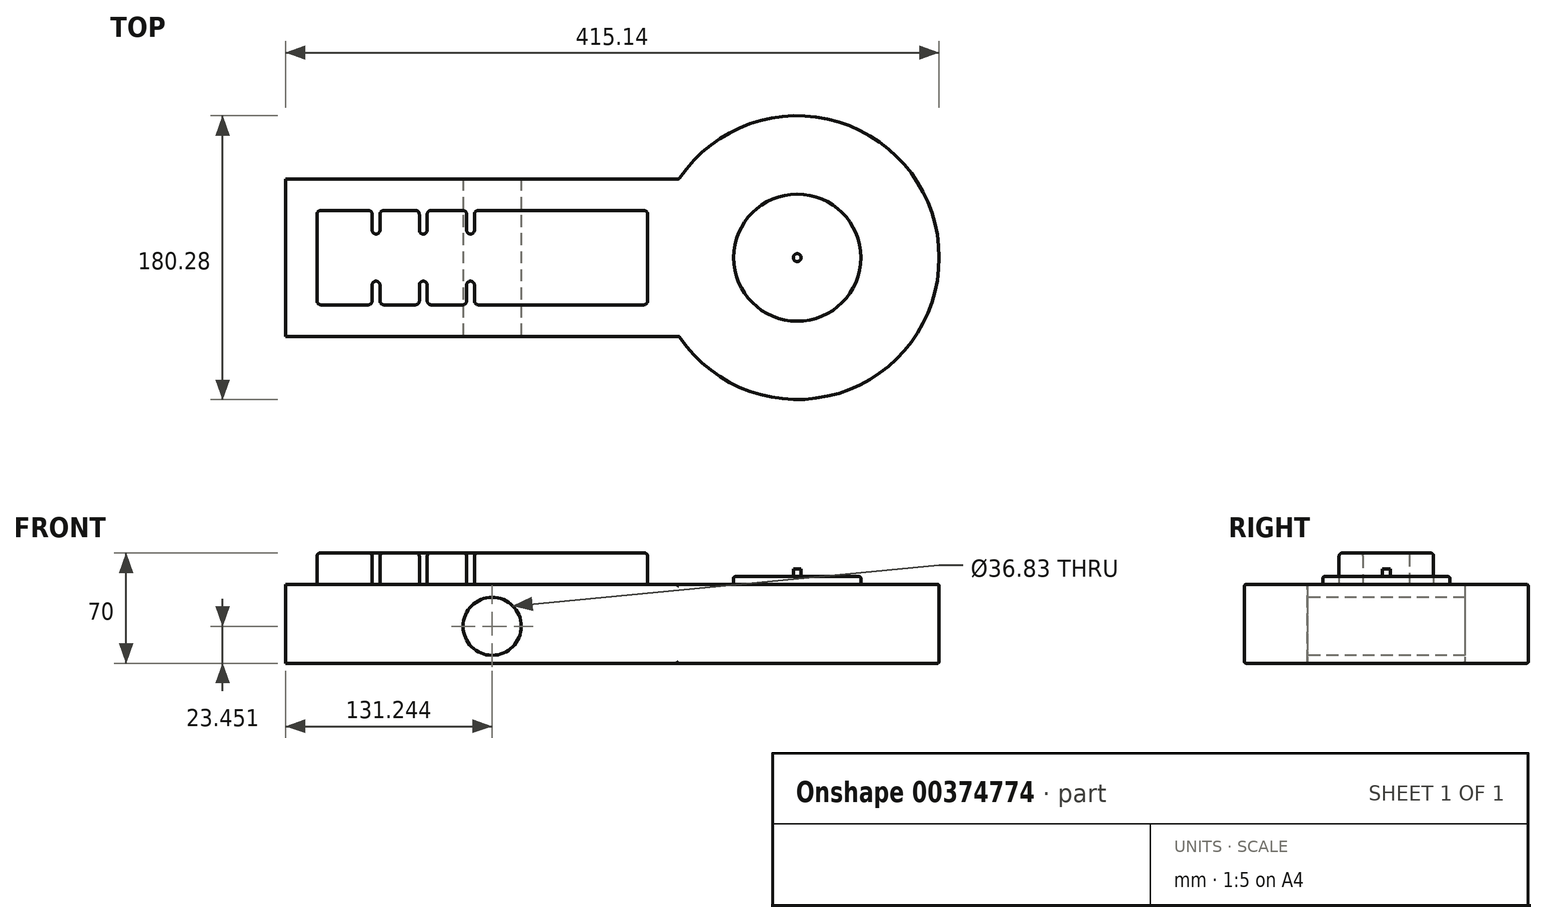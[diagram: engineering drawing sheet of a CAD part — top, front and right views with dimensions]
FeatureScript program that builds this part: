
annotation { "Feature Type Name" : "Feature", "Feature Type Description" : "" }
export const myFeature = defineFeature(function(context is Context, id is Id, definition is map)
    precondition{}
    {
        {
            var Q0;
            Q0=qCreatedBy(makeId("Top.planeOp"),FACE);
            var sketch = newSketch(context, id + "F0", { "sketchPlane" : qUnion([Q0])});
            skLineSegment(sketch, "E0.bottom", {"start": v(0, 0) * mm, "end": v(250, 0) * mm});
            skLineSegment(sketch, "E0.top", {"start": v(0, 100) * mm, "end": v(250, 100) * mm});
            skLineSegment(sketch, "E0.left", {"start": v(0, 0) * mm, "end": v(0, 100) * mm});
            skLineSegment(sketch, "E0.right", {"start": v(250, 0) * mm, "end": v(250, 100) * mm});
            skArc(sketch, "E1", {"start": v(250, 0) * mm, "mid": v(415.14, 50) * mm, "end": v(250, 100) * mm});
            skSolve(sketch);
        }
        {
            var Q0;
            Q0=makeQuery(id+"F0.imprint","IMPRINT",FACE,{"disambiguationData":[TD([[makeQuery(id+"F0.imprint","IMPRINT",EDGE,{"derivedFrom":sQuery(id+"F0.wireOp",EDGE,"E0.bottom")}),1.0]])]});
            var Q1;
            Q1=makeQuery(id+"F0.imprint","IMPRINT",FACE,{"disambiguationData":[TD([[makeQuery(id+"F0.imprint","IMPRINT",EDGE,{"derivedFrom":sQuery(id+"F0.wireOp",EDGE,"E0.right")}),-1.0]])]});
            extrude(context, id + "F1", {"entities" : qUnion([Q0, Q1]), "depth" : 50 * mm});
        }
        {
            var Q0;
            Q0=makeQuery(id+"F1.opExtrude","CAP_FACE",FACE,{"disambiguationData":[OSD([sQuery(id+"F0.wireOp",EDGE,"E0.bottom"),sQuery(id+"F0.wireOp",EDGE,"E0.top"),sQuery(id+"F0.wireOp",EDGE,"E0.left"),sQuery(id+"F0.wireOp",EDGE,"E1")])],"isStart":false});
            var sketch = newSketch(context, id + "F2", { "sketchPlane" : qUnion([Q0])});
            skLineSegment(sketch, "E2.bottom", {"start": v(20, 80) * mm, "end": v(230, 80) * mm});
            skLineSegment(sketch, "E2.top", {"start": v(20, 20) * mm, "end": v(230, 20) * mm});
            skLineSegment(sketch, "E2.left", {"start": v(20, 80) * mm, "end": v(20, 20) * mm});
            skLineSegment(sketch, "E2.right", {"start": v(230, 80) * mm, "end": v(230, 20) * mm});
            skLineSegment(sketch, "E3.bottom", {"start": v(55, 80) * mm, "end": v(60, 80) * mm});
            skLineSegment(sketch, "E3.top", {"start": v(55, 65) * mm, "end": v(60, 65) * mm});
            skLineSegment(sketch, "E3.left", {"start": v(55, 80) * mm, "end": v(55, 65) * mm});
            skLineSegment(sketch, "E3.right", {"start": v(60, 80) * mm, "end": v(60, 65) * mm});
            skLineSegment(sketch, "E4.bottom", {"start": v(85, 80) * mm, "end": v(90, 80) * mm});
            skLineSegment(sketch, "E4.top", {"start": v(85, 65) * mm, "end": v(90, 65) * mm});
            skLineSegment(sketch, "E4.left", {"start": v(85, 80) * mm, "end": v(85, 65) * mm});
            skLineSegment(sketch, "E4.right", {"start": v(90, 80) * mm, "end": v(90, 65) * mm});
            skLineSegment(sketch, "E5.bottom", {"start": v(115, 80) * mm, "end": v(120, 80) * mm});
            skLineSegment(sketch, "E5.top", {"start": v(115, 65) * mm, "end": v(120, 65) * mm});
            skLineSegment(sketch, "E5.left", {"start": v(115, 80) * mm, "end": v(115, 65) * mm});
            skLineSegment(sketch, "E5.right", {"start": v(120, 80) * mm, "end": v(120, 65) * mm});
            skLineSegment(sketch, "E6.bottom", {"start": v(55, 20) * mm, "end": v(60, 20) * mm});
            skLineSegment(sketch, "E6.top", {"start": v(55, 35) * mm, "end": v(60, 35) * mm});
            skLineSegment(sketch, "E6.left", {"start": v(55, 20) * mm, "end": v(55, 35) * mm});
            skLineSegment(sketch, "E6.right", {"start": v(60, 20) * mm, "end": v(60, 35) * mm});
            skLineSegment(sketch, "E7.bottom", {"start": v(85, 20) * mm, "end": v(90, 20) * mm});
            skLineSegment(sketch, "E7.top", {"start": v(85, 35) * mm, "end": v(90, 35) * mm});
            skLineSegment(sketch, "E7.left", {"start": v(85, 20) * mm, "end": v(85, 35) * mm});
            skLineSegment(sketch, "E7.right", {"start": v(90, 20) * mm, "end": v(90, 35) * mm});
            skLineSegment(sketch, "E8.bottom", {"start": v(115, 20) * mm, "end": v(120, 20) * mm});
            skLineSegment(sketch, "E8.top", {"start": v(115, 35) * mm, "end": v(120, 35) * mm});
            skLineSegment(sketch, "E8.left", {"start": v(115, 20) * mm, "end": v(115, 35) * mm});
            skLineSegment(sketch, "E8.right", {"start": v(120, 20) * mm, "end": v(120, 35) * mm});
            skSolve(sketch);
        }
        {
            var Q0;
            {var subQ20=sQuery(id+"F2.wireOp",EDGE,"E2.left");Q0=makeQuery(id+"F2.imprint","IMPRINT",FACE,{"disambiguationData":[TD([[makeQuery(id+"F2.imprint","IMPRINT",EDGE,{"derivedFrom":subQ20}),1.0]])]});}
            extrude(context, id + "F3", {"entities" : qUnion([Q0]), "operationType" : NewBodyOperationType.ADD, "depth" : 20 * mm});
        }
        {
            var Q0;
            Q0=makeQuery(id+"F1.opExtrude","CAP_FACE",FACE,{"disambiguationData":[OSD([sQuery(id+"F0.wireOp",EDGE,"E0.bottom"),sQuery(id+"F0.wireOp",EDGE,"E0.top"),sQuery(id+"F0.wireOp",EDGE,"E0.left"),sQuery(id+"F0.wireOp",EDGE,"E1")])],"isStart":false});
            var sketch = newSketch(context, id + "F4", { "sketchPlane" : qUnion([Q0])});
            skCircle(sketch, "E9", {"center": v(325, 50) * mm, "radius": 40.38 * mm});
            skSolve(sketch);
        }
        {
            var Q0;
            Q0=qSketchRegion(id+"F4",true);
            extrude(context, id + "F5", {"entities" : qUnion([Q0]), "operationType" : NewBodyOperationType.ADD, "depth" : 5 * mm});
        }
        {
            var Q0;
            Q0=makeQuery(id+"F5.opExtrude","CAP_FACE",FACE,{"disambiguationData":[OSD([sQuery(id+"F4.wireOp",EDGE,"E9")])],"isStart":false});
            var sketch = newSketch(context, id + "F6", { "sketchPlane" : qUnion([Q0])});
            skCircle(sketch, "E10", {"center": v(325, 50) * mm, "radius": 2.5 * mm});
            skSolve(sketch);
        }
        {
            var Q0;
            Q0=makeQuery(id+"F6.imprint","IMPRINT",FACE,{"disambiguationData":[TD([[makeQuery(id+"F6.imprint","IMPRINT",EDGE,{"derivedFrom":sQuery(id+"F6.wireOp",EDGE,"E10")}),1.0]])]});
            extrude(context, id + "F7", {"entities" : qUnion([Q0]), "operationType" : NewBodyOperationType.ADD, "depth" : 5 * mm});
        }
        {
            var Q0;
            Q0=makeQuery(id+"F1.opExtrude","SWEPT_FACE",FACE,{"disambiguationData":[OSD([sQuery(id+"F0.wireOp",EDGE,"E1")])]});
            var Q1;
            Q1=makeQuery(id+"F5.opExtrude","CAP_EDGE",EDGE,{"disambiguationData":[OSD([sQuery(id+"F4.wireOp",EDGE,"E9")])],"isStart":false});
            var Q2;
            Q2=makeQuery(id+"F5.opExtrude","CAP_EDGE",EDGE,{"disambiguationData":[OSD([sQuery(id+"F4.wireOp",EDGE,"E9")])],"isStart":true});
            fillet(context, id + "F8", {"entities" : qUnion([Q0, Q1, Q2]), "radius" : 1 * mm, "tangentPropagation" : true, "allowEdgeOverflow" : false});
        }
        {
            var Q0;
            Q0=makeQuery(id+"F3.opExtrude","SWEPT_EDGE",EDGE,{"disambiguationData":[OSD([sQuery(id+"F2.wireOp",EDGE,"E6.top"),sQuery(id+"F2.wireOp",EDGE,"E6.left")])]});
            var Q1;
            Q1=makeQuery(id+"F3.opExtrude","SWEPT_EDGE",EDGE,{"disambiguationData":[OSD([sQuery(id+"F2.wireOp",EDGE,"E2.top"),sQuery(id+"F2.wireOp",EDGE,"E6.bottom"),sQuery(id+"F2.wireOp",EDGE,"E6.left")])]});
            var Q2;
            Q2=makeQuery(id+"F3.opExtrude","SWEPT_EDGE",EDGE,{"disambiguationData":[OSD([sQuery(id+"F2.wireOp",EDGE,"E6.top"),sQuery(id+"F2.wireOp",EDGE,"E6.right")])]});
            var Q3;
            Q3=makeQuery(id+"F3.opExtrude","SWEPT_EDGE",EDGE,{"disambiguationData":[OSD([sQuery(id+"F2.wireOp",EDGE,"E2.top"),sQuery(id+"F2.wireOp",EDGE,"E6.bottom"),sQuery(id+"F2.wireOp",EDGE,"E6.right")])]});
            var Q4;
            Q4=makeQuery(id+"F3.opExtrude","SWEPT_EDGE",EDGE,{"disambiguationData":[OSD([sQuery(id+"F2.wireOp",EDGE,"E2.top"),sQuery(id+"F2.wireOp",EDGE,"E7.bottom"),sQuery(id+"F2.wireOp",EDGE,"E7.left")])]});
            var Q5;
            Q5=makeQuery(id+"F3.opExtrude","SWEPT_EDGE",EDGE,{"disambiguationData":[OSD([sQuery(id+"F2.wireOp",EDGE,"E7.top"),sQuery(id+"F2.wireOp",EDGE,"E7.right")])]});
            var Q6;
            Q6=makeQuery(id+"F3.opExtrude","SWEPT_EDGE",EDGE,{"disambiguationData":[OSD([sQuery(id+"F2.wireOp",EDGE,"E2.top"),sQuery(id+"F2.wireOp",EDGE,"E7.bottom"),sQuery(id+"F2.wireOp",EDGE,"E7.right")])]});
            var Q7;
            Q7=makeQuery(id+"F3.opExtrude","SWEPT_EDGE",EDGE,{"disambiguationData":[OSD([sQuery(id+"F2.wireOp",EDGE,"E2.top"),sQuery(id+"F2.wireOp",EDGE,"E8.bottom"),sQuery(id+"F2.wireOp",EDGE,"E8.left")])]});
            var Q8;
            Q8=makeQuery(id+"F3.opExtrude","SWEPT_EDGE",EDGE,{"disambiguationData":[OSD([sQuery(id+"F2.wireOp",EDGE,"E8.top"),sQuery(id+"F2.wireOp",EDGE,"E8.right")])]});
            var Q9;
            Q9=makeQuery(id+"F3.opExtrude","SWEPT_EDGE",EDGE,{"disambiguationData":[OSD([sQuery(id+"F2.wireOp",EDGE,"E2.top"),sQuery(id+"F2.wireOp",EDGE,"E8.bottom"),sQuery(id+"F2.wireOp",EDGE,"E8.right")])]});
            var Q10;
            Q10=makeQuery(id+"F3.opExtrude","SWEPT_EDGE",EDGE,{"disambiguationData":[OSD([sQuery(id+"F2.wireOp",EDGE,"E7.top"),sQuery(id+"F2.wireOp",EDGE,"E7.left")])]});
            var Q11;
            Q11=makeQuery(id+"F3.opExtrude","SWEPT_EDGE",EDGE,{"disambiguationData":[OSD([sQuery(id+"F2.wireOp",EDGE,"E8.top"),sQuery(id+"F2.wireOp",EDGE,"E8.left")])]});
            var Q12;
            Q12=makeQuery(id+"F3.opExtrude","SWEPT_EDGE",EDGE,{"disambiguationData":[OSD([sQuery(id+"F2.wireOp",EDGE,"E3.top"),sQuery(id+"F2.wireOp",EDGE,"E3.left")])]});
            var Q13;
            Q13=makeQuery(id+"F3.opExtrude","SWEPT_EDGE",EDGE,{"disambiguationData":[OSD([sQuery(id+"F2.wireOp",EDGE,"E2.bottom"),sQuery(id+"F2.wireOp",EDGE,"E3.bottom"),sQuery(id+"F2.wireOp",EDGE,"E3.left")])]});
            var Q14;
            Q14=makeQuery(id+"F3.opExtrude","SWEPT_EDGE",EDGE,{"disambiguationData":[OSD([sQuery(id+"F2.wireOp",EDGE,"E4.top"),sQuery(id+"F2.wireOp",EDGE,"E4.left")])]});
            var Q15;
            Q15=makeQuery(id+"F3.opExtrude","SWEPT_EDGE",EDGE,{"disambiguationData":[OSD([sQuery(id+"F2.wireOp",EDGE,"E2.bottom"),sQuery(id+"F2.wireOp",EDGE,"E4.bottom"),sQuery(id+"F2.wireOp",EDGE,"E4.left")])]});
            var Q16;
            Q16=makeQuery(id+"F3.opExtrude","SWEPT_EDGE",EDGE,{"disambiguationData":[OSD([sQuery(id+"F2.wireOp",EDGE,"E5.top"),sQuery(id+"F2.wireOp",EDGE,"E5.left")])]});
            var Q17;
            Q17=makeQuery(id+"F3.opExtrude","SWEPT_EDGE",EDGE,{"disambiguationData":[OSD([sQuery(id+"F2.wireOp",EDGE,"E2.bottom"),sQuery(id+"F2.wireOp",EDGE,"E5.bottom"),sQuery(id+"F2.wireOp",EDGE,"E5.left")])]});
            var Q18;
            Q18=makeQuery(id+"F3.opExtrude","SWEPT_EDGE",EDGE,{"disambiguationData":[OSD([sQuery(id+"F2.wireOp",EDGE,"E3.top"),sQuery(id+"F2.wireOp",EDGE,"E3.right")])]});
            var Q19;
            Q19=makeQuery(id+"F3.opExtrude","SWEPT_EDGE",EDGE,{"disambiguationData":[OSD([sQuery(id+"F2.wireOp",EDGE,"E2.bottom"),sQuery(id+"F2.wireOp",EDGE,"E3.bottom"),sQuery(id+"F2.wireOp",EDGE,"E3.right")])]});
            var Q20;
            Q20=makeQuery(id+"F3.opExtrude","SWEPT_EDGE",EDGE,{"disambiguationData":[OSD([sQuery(id+"F2.wireOp",EDGE,"E4.top"),sQuery(id+"F2.wireOp",EDGE,"E4.right")])]});
            var Q21;
            Q21=makeQuery(id+"F3.opExtrude","SWEPT_EDGE",EDGE,{"disambiguationData":[OSD([sQuery(id+"F2.wireOp",EDGE,"E2.bottom"),sQuery(id+"F2.wireOp",EDGE,"E4.bottom"),sQuery(id+"F2.wireOp",EDGE,"E4.right")])]});
            var Q22;
            Q22=makeQuery(id+"F3.opExtrude","SWEPT_EDGE",EDGE,{"disambiguationData":[OSD([sQuery(id+"F2.wireOp",EDGE,"E5.top"),sQuery(id+"F2.wireOp",EDGE,"E5.right")])]});
            var Q23;
            Q23=makeQuery(id+"F3.opExtrude","SWEPT_EDGE",EDGE,{"disambiguationData":[OSD([sQuery(id+"F2.wireOp",EDGE,"E2.bottom"),sQuery(id+"F2.wireOp",EDGE,"E5.bottom"),sQuery(id+"F2.wireOp",EDGE,"E5.right")])]});
            var Q24;
            Q24=makeQuery(id+"F3.opExtrude","SWEPT_EDGE",EDGE,{"disambiguationData":[OSD([sQuery(id+"F2.wireOp",EDGE,"E2.bottom"),sQuery(id+"F2.wireOp",EDGE,"E2.left")])]});
            var Q25;
            Q25=makeQuery(id+"F3.opExtrude","SWEPT_EDGE",EDGE,{"disambiguationData":[OSD([sQuery(id+"F2.wireOp",EDGE,"E2.top"),sQuery(id+"F2.wireOp",EDGE,"E2.left")])]});
            var Q26;
            Q26=makeQuery(id+"F3.opExtrude","SWEPT_EDGE",EDGE,{"disambiguationData":[OSD([sQuery(id+"F2.wireOp",EDGE,"E2.bottom"),sQuery(id+"F2.wireOp",EDGE,"E2.right")])]});
            var Q27;
            Q27=makeQuery(id+"F3.opExtrude","SWEPT_EDGE",EDGE,{"disambiguationData":[OSD([sQuery(id+"F2.wireOp",EDGE,"E2.top"),sQuery(id+"F2.wireOp",EDGE,"E2.right")])]});
            fillet(context, id + "F9", {"entities" : qUnion([Q0, Q1, Q2, Q3, Q4, Q5, Q6, Q7, Q8, Q9, Q10, Q11, Q12, Q13, Q14, Q15, Q16, Q17, Q18, Q19, Q20, Q21, Q22, Q23, Q24, Q25, Q26, Q27]), "radius" : 2.5 * mm, "tangentPropagation" : true, "allowEdgeOverflow" : false});
        }
        {
            var Q0;
            {var subQ0=sQuery(id+"F2.wireOp",EDGE,"E2.bottom");Q0=makeQuery(id+"F3.opExtrude","CAP_EDGE",EDGE,{"disambiguationData":[OSD([subQ0]),TDD([makeQuery(id+"F2.imprint","IMPRINT",EDGE,{"disambiguationData":[TD([[makeQuery(id+"F2.imprint","INTERSECT",VERTEX,{"derivedFrom":[subQ0,sQuery(id+"F2.wireOp",EDGE,"E2.right")]}),1.0]])],"derivedFrom":subQ0})])],"isStart":false});}
            var Q1;
            Q1=makeQuery(id+"F3.opExtrude","CAP_EDGE",EDGE,{"disambiguationData":[OSD([sQuery(id+"F2.wireOp",EDGE,"E2.right")])],"isStart":false});
            fillet(context, id + "F10", {"entities" : qUnion([Q0, Q1]), "radius" : 2 * mm, "tangentPropagation" : true, "allowEdgeOverflow" : false});
        }
        {
            var Q0;
            Q0=makeQuery(id+"F1.opExtrude","SWEPT_FACE",FACE,{"disambiguationData":[OSD([sQuery(id+"F0.wireOp",EDGE,"E0.bottom")])]});
            var sketch = newSketch(context, id + "F11", { "sketchPlane" : qUnion([Q0])});
            skCircle(sketch, "E11", {"center": v(131.24, 23.45) * mm, "radius": 18.41 * mm});
            skSolve(sketch);
        }
        {
            var Q0;
            Q0 = qSketchRegion(id + "F11", true);
            extrude(context, id + "F12", {"entities" : qUnion([Q0]), "operationType" : NewBodyOperationType.ADD, "depth" : 25 * mm});
        }
        {
            var Q0;
            Q0=makeQuery(id+"F12.opExtrude","CAP_FACE",FACE,{"disambiguationData":[OSD([sQuery(id+"F11.wireOp",EDGE,"E11")])],"isStart":false});
            extrude(context, id + "F13", {"entities" : qUnion([Q0]), "operationType" : NewBodyOperationType.REMOVE, "endBound" : BoundingType.THROUGH_ALL, "oppositeDirection" : true, "depth" : 25 * mm});
        }
    });
